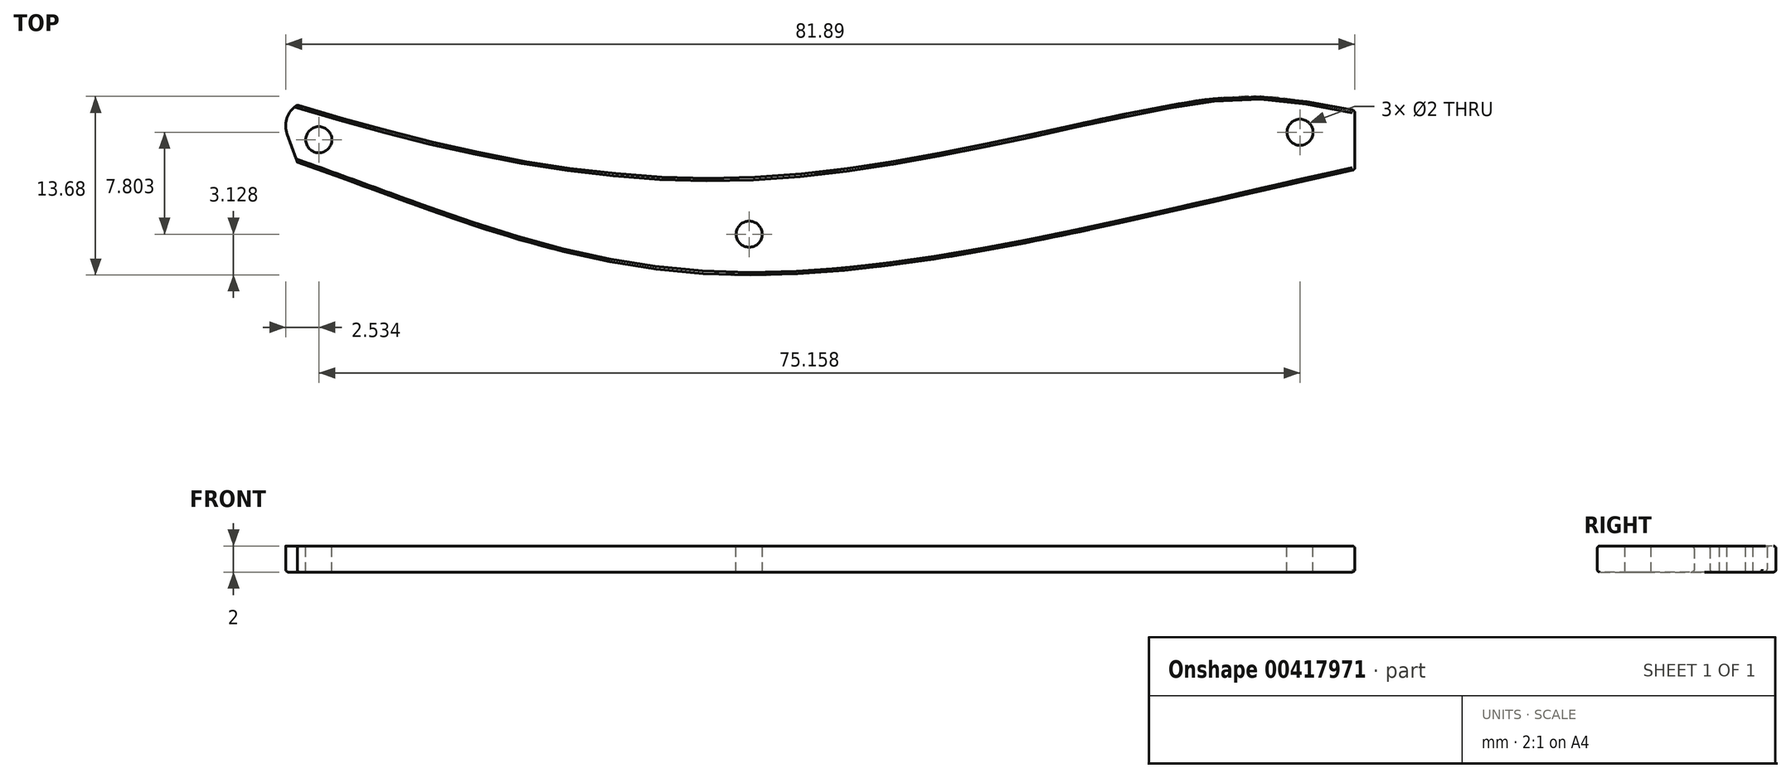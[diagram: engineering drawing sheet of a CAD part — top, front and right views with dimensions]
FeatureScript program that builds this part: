
annotation { "Feature Type Name" : "Feature", "Feature Type Description" : "" }
export const myFeature = defineFeature(function(context is Context, id is Id, definition is map)
    precondition{}
    {
        {
            var Q0;
            Q0=qCreatedBy(makeId("Top.planeOp"),FACE);
            var sketch = newSketch(context, id + "F0", { "sketchPlane" : qUnion([Q0])});
            skFitSpline(sketch, "E0", {"points": [v(-23.45, 10.12) * mm, v(12.79, 4.66) * mm, v(48, 10.72) * mm, v(57.55, 9.7) * mm], "startDerivative": vector(80.73, -24.3) * mm, "endDerivative": vector(47.68, -7.36) * mm});
            skFitSpline(sketch, "E1", {"points": [v(-23.45, 5.74) * mm, v(7.79, -2.8) * mm, v(57.55, 5.16) * mm], "startDerivative": vector(66.3, -22.9) * mm, "endDerivative": vector(94.86, 20.77) * mm});
            skLineSegment(sketch, "E2", {"start": v(57.55, 5.16) * mm, "end": v(57.55, 9.7) * mm});
            skLineSegment(sketch, "E3", {"start": v(-23.45, 5.74) * mm, "end": v(-24.23, 7.9) * mm});
            skArc(sketch, "E4", {"start": v(-23.45, 10.12) * mm, "mid": v(-24.23, 9.15) * mm, "end": v(-24.23, 7.9) * mm});
            skSolve(sketch);
        }
        {
            var Q0;
            Q0=makeQuery(id+"F0.imprint","IMPRINT",FACE,{"disambiguationData":[TD([[makeQuery(id+"F0.imprint","IMPRINT",EDGE,{"derivedFrom":sQuery(id+"F0.wireOp",EDGE,"E0")}),-1.0]])]});
            extrude(context, id + "F1", {"entities" : qUnion([Q0]), "depth" : 2 * mm});
        }
        {
            var Q0;
            Q0=makeQuery(id+"F1.opExtrude","CAP_EDGE",EDGE,{"disambiguationData":[OSD([sQuery(id+"F0.wireOp",EDGE,"E1")])],"isStart":true});
            var Q1;
            Q1=makeQuery(id+"F1.opExtrude","CAP_EDGE",EDGE,{"disambiguationData":[OSD([sQuery(id+"F0.wireOp",EDGE,"E3")])],"isStart":true});
            var Q2;
            Q2=makeQuery(id+"F1.opExtrude","CAP_EDGE",EDGE,{"disambiguationData":[OSD([sQuery(id+"F0.wireOp",EDGE,"E4")])],"isStart":true});
            var Q3;
            Q3=makeQuery(id+"F1.opExtrude","SWEPT_EDGE",EDGE,{"disambiguationData":[OSD([sQuery(id+"F0.wireOp",EDGE,"E0"),sQuery(id+"F0.wireOp",EDGE,"E4")])]});
            var Q4;
            Q4=makeQuery(id+"F1.opExtrude","CAP_EDGE",EDGE,{"disambiguationData":[OSD([sQuery(id+"F0.wireOp",EDGE,"E0")])],"isStart":true});
            var Q5;
            Q5=makeQuery(id+"F1.opExtrude","CAP_EDGE",EDGE,{"disambiguationData":[OSD([sQuery(id+"F0.wireOp",EDGE,"E0")])],"isStart":false});
            var Q6;
            Q6=makeQuery(id+"F1.opExtrude","CAP_EDGE",EDGE,{"disambiguationData":[OSD([sQuery(id+"F0.wireOp",EDGE,"E2")])],"isStart":true});
            var Q7;
            Q7=makeQuery(id+"F1.opExtrude","CAP_EDGE",EDGE,{"disambiguationData":[OSD([sQuery(id+"F0.wireOp",EDGE,"E2")])],"isStart":false});
            var Q8;
            Q8=makeQuery(id+"F1.opExtrude","CAP_EDGE",EDGE,{"disambiguationData":[OSD([sQuery(id+"F0.wireOp",EDGE,"E1")])],"isStart":false});
            var Q9;
            Q9=makeQuery(id+"F1.opExtrude","SWEPT_EDGE",EDGE,{"disambiguationData":[OSD([sQuery(id+"F0.wireOp",EDGE,"E1"),sQuery(id+"F0.wireOp",EDGE,"E2")])]});
            var Q10;
            Q10=makeQuery(id+"F1.opExtrude","SWEPT_EDGE",EDGE,{"disambiguationData":[OSD([sQuery(id+"F0.wireOp",EDGE,"E0"),sQuery(id+"F0.wireOp",EDGE,"E2")])]});
            fillet(context, id + "F2", {"entities" : qUnion([Q0, Q1, Q2, Q3, Q4, Q5, Q6, Q7, Q8, Q9, Q10]), "radius" : 0.2 * mm, "tangentPropagation" : true, "allowEdgeOverflow" : false});
        }
        {
            var Q0;
            Q0=makeQuery(id+"F1.opExtrude","CAP_FACE",FACE,{"disambiguationData":[OSD([sQuery(id+"F0.wireOp",EDGE,"E0"),sQuery(id+"F0.wireOp",EDGE,"E1"),sQuery(id+"F0.wireOp",EDGE,"E2"),sQuery(id+"F0.wireOp",EDGE,"E3"),sQuery(id+"F0.wireOp",EDGE,"E4")])],"isStart":false});
            var sketch = newSketch(context, id + "F3", { "sketchPlane" : qUnion([Q0])});
            skCircle(sketch, "E5", {"center": v(-21.8, 7.46) * mm, "radius": 1 * mm});
            skCircle(sketch, "E6", {"center": v(11.16, 0.23) * mm, "radius": 1 * mm});
            skCircle(sketch, "E7", {"center": v(53.35, 8.03) * mm, "radius": 1 * mm});
            skSolve(sketch);
        }
        {
            var Q0;
            Q0=makeQuery(id+"F3.imprint","IMPRINT",FACE,{"disambiguationData":[TD([[makeQuery(id+"F3.imprint","IMPRINT",EDGE,{"derivedFrom":sQuery(id+"F3.wireOp",EDGE,"E5")}),1.0]])]});
            var Q1;
            Q1=makeQuery(id+"F3.imprint","IMPRINT",FACE,{"disambiguationData":[TD([[makeQuery(id+"F3.imprint","IMPRINT",EDGE,{"derivedFrom":sQuery(id+"F3.wireOp",EDGE,"E7")}),1.0]])]});
            var Q2;
            Q2=makeQuery(id+"F3.imprint","IMPRINT",FACE,{"disambiguationData":[TD([[makeQuery(id+"F3.imprint","IMPRINT",EDGE,{"derivedFrom":sQuery(id+"F3.wireOp",EDGE,"E6")}),1.0]])]});
            extrude(context, id + "F4", {"entities" : qUnion([Q0, Q1, Q2]), "operationType" : NewBodyOperationType.REMOVE, "oppositeDirection" : true, "depth" : 25 * mm});
        }
    });
